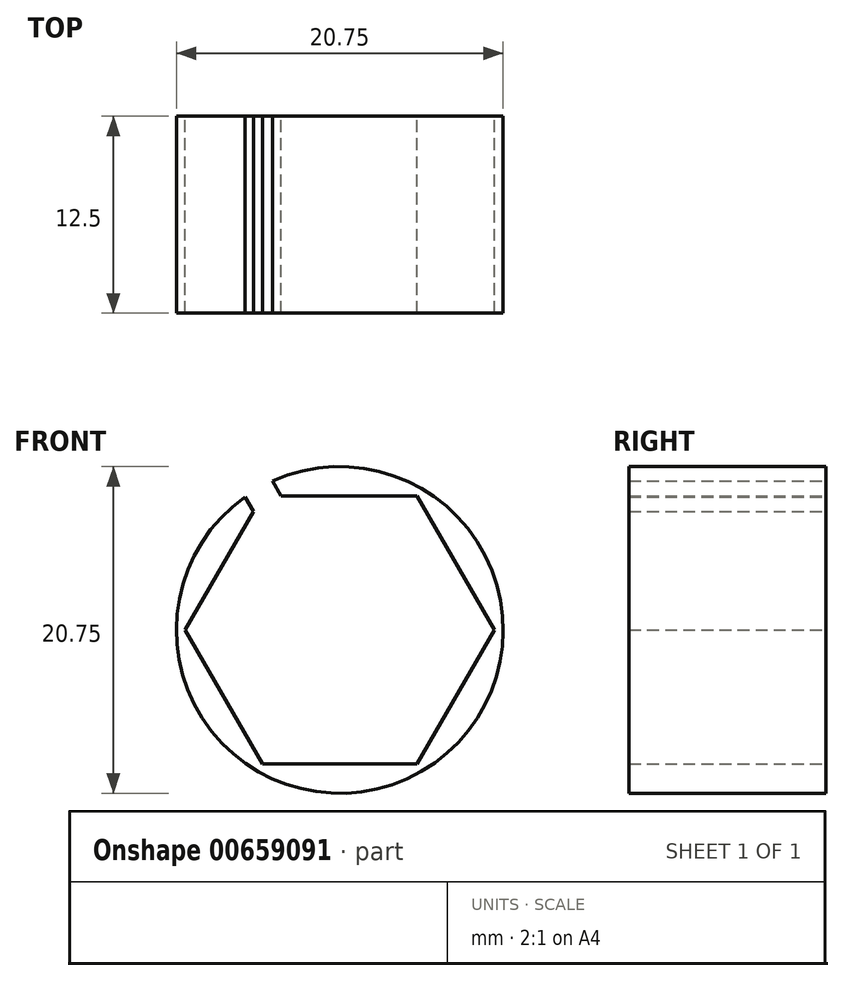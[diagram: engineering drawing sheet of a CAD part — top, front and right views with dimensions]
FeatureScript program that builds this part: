
annotation { "Feature Type Name" : "Feature", "Feature Type Description" : "" }
export const myFeature = defineFeature(function(context is Context, id is Id, definition is map)
    precondition{}
    {
        {
            var Q0;
            Q0=qCreatedBy(makeId("Front.planeOp"),FACE);
            var sketch = newSketch(context, id + "F0", { "sketchPlane" : qUnion([Q0])});
            skCircle(sketch, "E0.cCircle", {"center": v(0, 0) * mm, "radius": 8.5 * mm, "construction": true});
            skLineSegment(sketch, "E0.0", {"start": v(9.81, 0) * mm, "end": v(4.9, -8.5) * mm});
            skLineSegment(sketch, "E0.1", {"start": v(4.9, -8.5) * mm, "end": v(-4.9, -8.5) * mm});
            skLineSegment(sketch, "E0.2", {"start": v(-4.9, -8.5) * mm, "end": v(-9.81, 0) * mm});
            skLineSegment(sketch, "E0.3", {"start": v(-9.81, 0) * mm, "end": v(-5.47, 7.52) * mm});
            skLineSegment(sketch, "E0.4", {"start": v(-4.9, 8.5) * mm, "end": v(-4.88, 8.5) * mm});
            skLineSegment(sketch, "E0.5", {"start": v(4.9, 8.5) * mm, "end": v(9.81, 0) * mm});
            skPoint(sketch, "E0.0.midPoint", {"position": v(7.36, -4.25) * mm});
            skArc(sketch, "E1", {"start": v(-6.01, 8.46) * mm, "mid": v(5.17, -9) * mm, "end": v(-4.28, 9.45) * mm});
            skLineSegment(sketch, "E2.0.left", {"start": v(-5.47, 7.52) * mm, "end": v(-6.01, 8.46) * mm});
            skLineSegment(sketch, "E2.0.right", {"start": v(-3.73, 8.5) * mm, "end": v(-4.28, 9.45) * mm});
            skLineSegment(sketch, "E3.trimOffspring", {"start": v(-3.73, 8.5) * mm, "end": v(4.9, 8.5) * mm});
            skSolve(sketch);
        }
        {
            var Q0;
            Q0=makeQuery(id+"F0.imprint","IMPRINT",FACE,{"disambiguationData":[TD([[makeQuery(id+"F0.imprint","IMPRINT",EDGE,{"derivedFrom":sQuery(id+"F0.wireOp",EDGE,"E0.0")}),1.0]])]});
            extrude(context, id + "F1", {"entities" : qUnion([Q0]), "depth" : 12.5 * mm, "offsetDistance" : 25 * mm});
        }
    });
